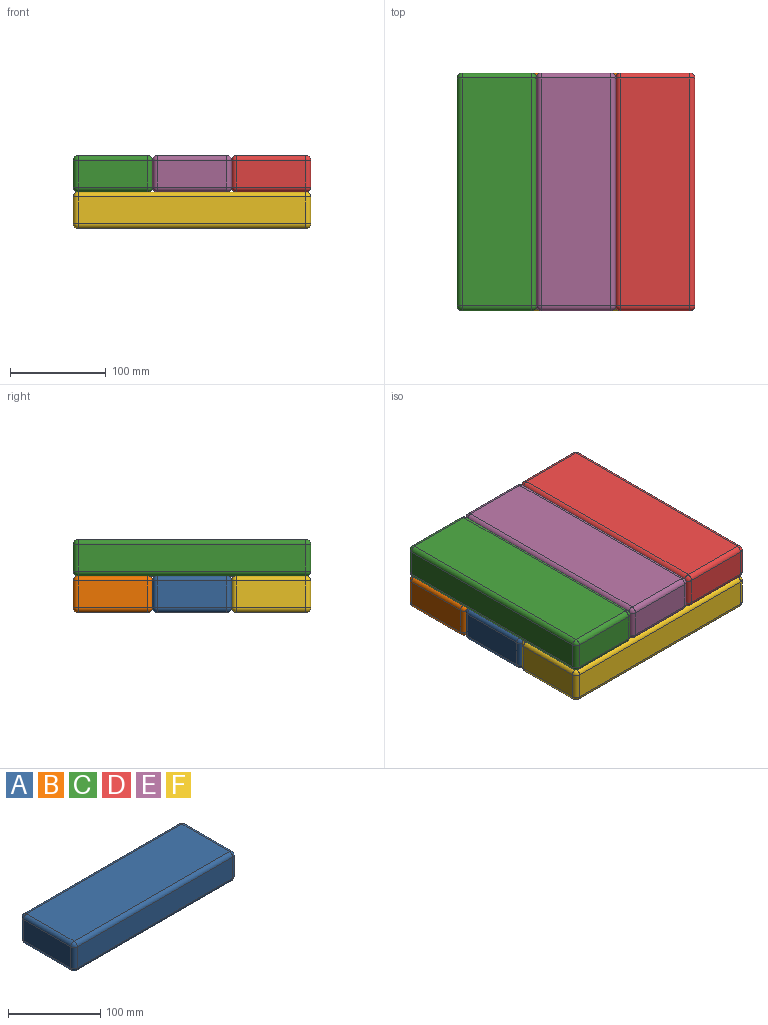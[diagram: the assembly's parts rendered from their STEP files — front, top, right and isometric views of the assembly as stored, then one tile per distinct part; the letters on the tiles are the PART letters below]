
ASSEMBLY  parts=6 mates=1
PART A: 26 faces, bbox 247.7x82.6x38.1 mm
  f0: plane 237.49x72.39mm, normal (0,0,1), area 17191.9mm2, adj f14,f19,f22,f25
  f1: plane 237.49x27.94mm, normal (0,-1,0), area 6635.5mm2, adj f11,f20,f21,f25
  f2: plane 237.49x72.39mm, normal (0,0,-1), area 17191.9mm2, adj f6,f10,f11,f12
  f3: plane 237.49x27.94mm, normal (0,1,0), area 6635.5mm2, adj f6,f9,f13,f14
  f4: plane 72.39x27.94mm, normal (1,0,0), area 2022.6mm2, adj f9,f10,f19,f20
  f5: plane 72.39x27.94mm, normal (-1,0,0), area 2022.6mm2, adj f12,f13,f21,f22
  f6: cylinder r=5.08mm len=237.49mm, axis (1,0,0), area 1895.1mm2, adj f2,f3,f7,f8
  f7: sphere r=5.08mm, area 40.5mm2, adj f6,f9,f10
  f8: sphere r=5.08mm, area 40.5mm2, adj f6,f12,f13
  f9: cylinder r=5.08mm len=27.94mm, axis (0,0,-1), area 223mm2, adj f3,f4,f7,f15
  f10: cylinder r=5.08mm len=72.39mm, axis (0,-1,0), area 577.6mm2, adj f2,f4,f7,f16
  f11: cylinder r=5.08mm len=237.49mm, axis (-1,0,0), area 1895.1mm2, adj f1,f2,f16,f17
  f12: cylinder r=5.08mm len=72.39mm, axis (0,1,0), area 577.6mm2, adj f2,f5,f8,f17
  f13: cylinder r=5.08mm len=27.94mm, axis (0,0,1), area 223mm2, adj f3,f5,f8,f18
  f14: cylinder r=5.08mm len=237.49mm, axis (-1,0,0), area 1895.1mm2, adj f0,f3,f15,f18
  f15: sphere r=5.08mm, area 40.5mm2, adj f9,f14,f19
  f16: sphere r=5.08mm, area 40.5mm2, adj f10,f11,f20
  f17: sphere r=5.08mm, area 40.5mm2, adj f11,f12,f21
  f18: sphere r=5.08mm, area 40.5mm2, adj f13,f14,f22
  f19: cylinder r=5.08mm len=72.39mm, axis (0,1,0), area 577.6mm2, adj f0,f4,f15,f23
  f20: cylinder r=5.08mm len=27.94mm, axis (0,0,1), area 223mm2, adj f1,f4,f16,f23
  f21: cylinder r=5.08mm len=27.94mm, axis (0,0,-1), area 223mm2, adj f1,f5,f17,f24
  f22: cylinder r=5.08mm len=72.39mm, axis (0,-1,0), area 577.6mm2, adj f0,f5,f18,f24
  f23: sphere r=5.08mm, area 40.5mm2, adj f19,f20,f25
  f24: sphere r=5.08mm, area 40.5mm2, adj f21,f22,f25
  f25: cylinder r=5.08mm len=237.49mm, axis (1,0,0), area 1895.1mm2, adj f0,f1,f23,f24
PART B: same geometry as A
PART C: same geometry as A
PART D: same geometry as A
PART E: same geometry as A
PART F: same geometry as A
PLACE A t=(3.87,105.44,47.39)mm
PLACE B t=(3.87,187.99,47.39)mm
PLACE C rot(axis=(0,0,1),90deg) t=(-78.68,105.44,85.49)mm
PLACE D rot(axis=(0,0,1),90deg) t=(86.42,105.44,85.49)mm
PLACE E rot(axis=(0,0,1),90deg) t=(3.87,105.44,85.49)mm
PLACE F t=(3.87,22.89,47.39)mm
MATE fastened E.f2 <-> A.f0  axis (0,0,-1) through (3.87,105.44,66.44)mm
